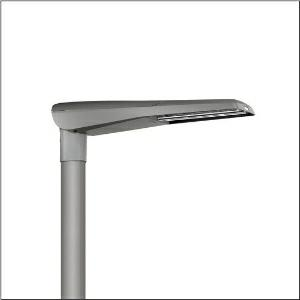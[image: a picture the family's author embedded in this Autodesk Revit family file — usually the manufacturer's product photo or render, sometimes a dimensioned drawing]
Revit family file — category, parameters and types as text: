
# Revit family: streetlight_sl_11_iq_mini___st1_2p1_0_5xc2gc1f08ge_d462
name_source: partatom
category: Lighting Fixtures
units: mm (PartAtom-declared; Revit-internal decimal feet)

## family parameters
Cut with Voids When Loaded = No
Host = Face
Light Source = No
Part Type = Normal
Room Calculation Point = No
Round Connector Dimension = Use Diameter
Shared = No

## types (1)
- --- (1 x LED, 2960 lm, 24.7 W, 2200K)
    Apparent Load = 25 VA
    CIE Flux Codes = 31 68 95 100 100
    Color Rendering = 70
    Color Temperature = 2200K
    Default Elevation = 1800 mm
    Description = Streetlight SL 11 iQ mini, mast luminaire, primary light control with 3 zone facetted reflector, of plastic, silver coated, highly specular, primary optical cover: cover, of PMMA, transparent, light distribution: ST1.2P1.0, light emission: direct distribution, primary light characteristic: asymmetric, installation type: post-top, side-entry, lamps: LED, High Power LED, rated values: 3.480lm | 24,3W | 143,2lm/W (begin service life); end service life: 3.480lm | 25W; at 50% lumin. flux: 1.740lm | 12,5W | 139,2lm/W, colour temperature: 2200/2700/3000/4000K, colour rendering: CRI > 70, light colour: 722/727/730/740, light setting 1 begin service life: 100% | 3.480lm | 24,3W | 143,2lm/W | 3.000K, light setting 1 end service life: 25W, further light settings possible, control: Street-Remote, Auto-Match, Temp-Guard, Lumen-Switch, Night-Set, Smart-Wire, Light-Fading, Desk-Remote (wireless, voltage-free reading and setting of iQ features in the workshop via application-optimized NFC function/RFID function), optimised constant luminous flux control (CLO 2.0), with cable H07RN-F 3x 1.5mm², mains connection: 230..240V, AC, 50/60Hz, connection cable pre-assembled, cable length: 6,5m, luminaire housing, of diecast aluminium, powder-coated, SITECO metallic grey (DB 702S), please order mast flange separately, inclination adjustable without tools: 0°, 5°, 10°, 15° (post-top) | 0°, -5°, -10°, -15° (side-entry), sealing non-destructively replaceable, multi-level sealing system, length: 736mm, width: 174mm, height: 116mm, mast flange for spigot size: 42mm (side-entry): 5XC10008XM4, 60/48mm (side-entry/post-top): 5XC10108XM2, 76/60mm (side-entry/post-top): 5XC10108XM1, equipment: standard, protection rating (complete): IP66, insulation class (complete): insulation class II (safety insulation), certification: CE, ENEC, ENEC+, VDE, impact resistance: IK10, permissible operating ambient temperature for outdoor applications: -25..+50°C, standard-compliant lighting for roads and squares, Environmental Product Declaration (EPD) tested and certified by an independent institute, packaging unit: 1 piece

Light Distribution: ST1.2P1.0
    Height = 116 mm
    Lamp = 1 x LED
    Lamp Light Flux = 2960 lm
    Lamp Power = 24.7 W
    Lamp count = 1
    Length = 736 mm
    Luminous efficacy = 120 lm/W
    Manufacturer = Siteco
    ModVariant = No
    Model = 5XC2GC1F08GE
    Number of Poles = 1
    OnlyDefault = Yes
    Power Factor = 1
    Product Name = Streetlight SL 11 iQ mini | ST1.2P1.0
    Product group = mast luminaire | pylon top
    ProductGroupID = 6100
    Protection Class = Protection class II
    Protection Degree = IP 66
    RLX_Detail_Level = 1
    RLX_Emergency_Light_Flux = 0 lm
    RLX_Emergency_Type = 0
    RLX_Emergency_Type_DB = No
    RlxData = <blob elided: 53121 chars, md5=cc1b53e3>
    Socket = socket
    Standby Power = 0 W
    System Light Flux = 2960 lm
    System Power = 25 W
    Type Comments = individual setting: luminous flux: 100 % | dim-lin: 254 | 342 mA
    Type Image = l_1003508.jpg
    URL = http://relux.com
    VarID = @adj_041561
    Voltage = 0 V
    Weight = 0.00 kg
    Width = 174 mm

## geometry (parser evidence)
native form markers: Blend x4, Sweep x12
no freeform markers — native parametric forms only
